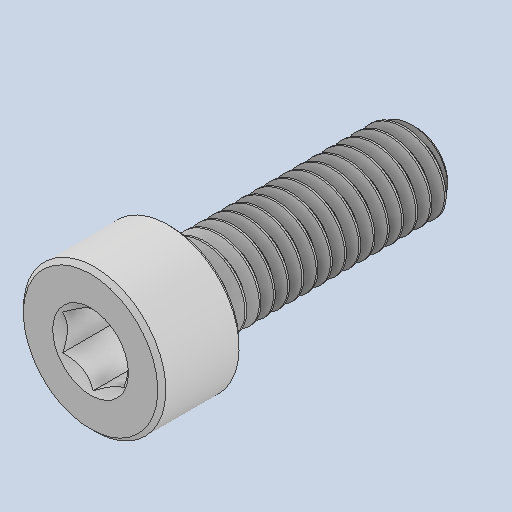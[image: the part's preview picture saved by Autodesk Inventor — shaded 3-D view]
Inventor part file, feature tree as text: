
AUTODESK INVENTOR PART (.ipt)
format: ipt  version: 2025.1 (Build 291241020, 241B)  size: 508,416 bytes
history: native  units: in
note: dims shown in document units (in); Inventor stores cm internally (conversion verified against a paired STEP export)
features: revolve x1
ambient origin geometry x8: Origin, YZ Plane, XZ Plane, XY Plane, X Axis, Y Axis, Z Axis, Center Point
bodies: Solid1 (feature_tree)
feature tree (1):
  revolve  "Revolve2"  [1 undecoded]
note: 1 required parameter value undecoded (feature->parameter linkage not recoverable at this tier; creation-order binding heuristic only, values carry confidence <= 0.55)
